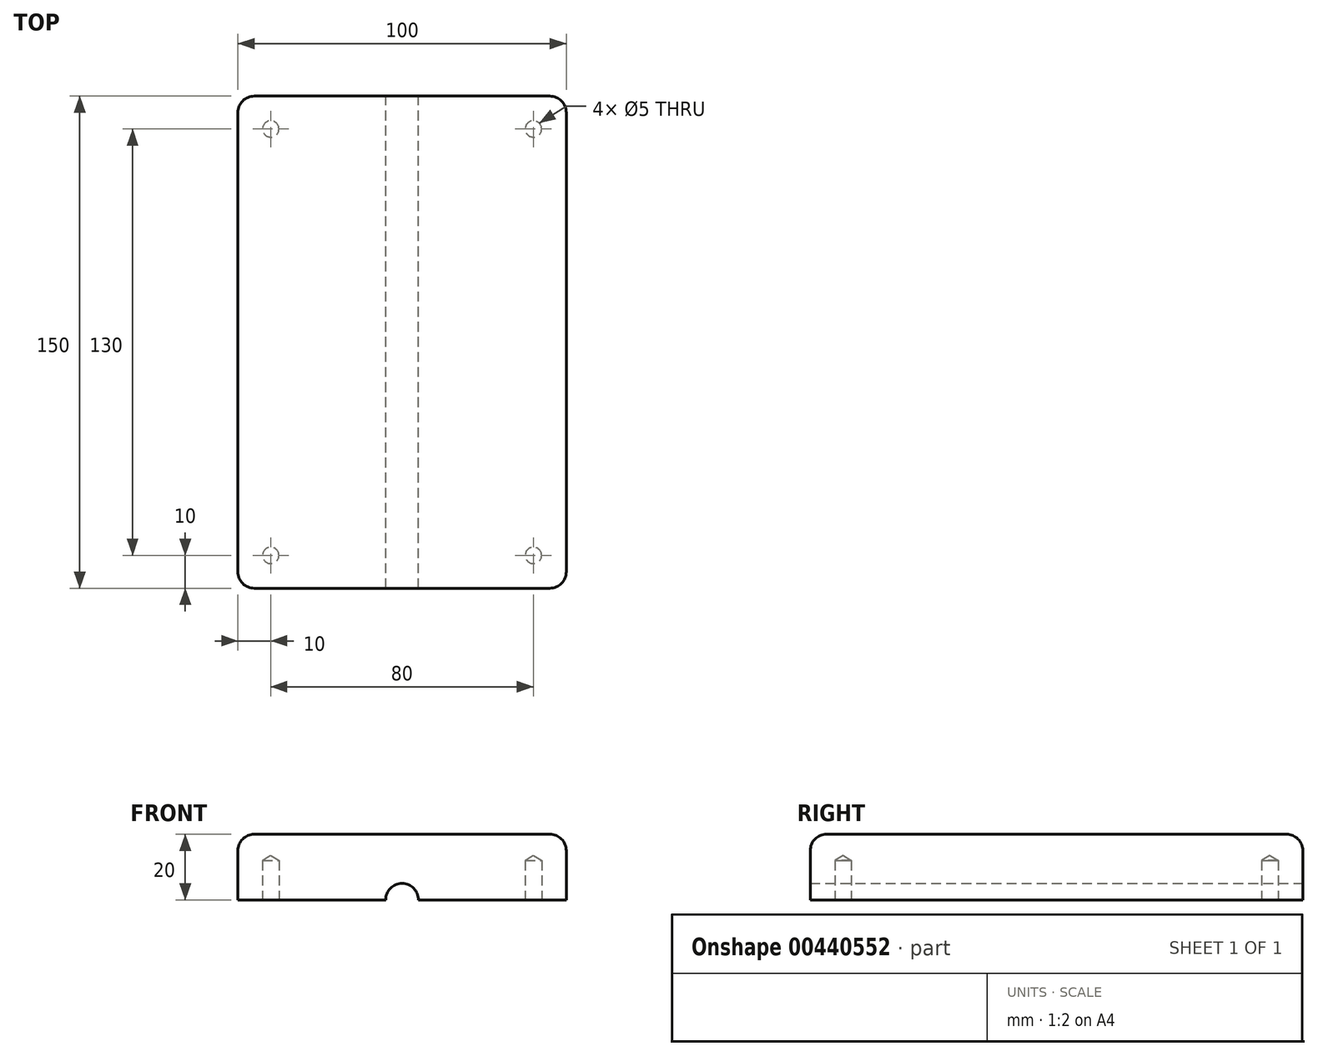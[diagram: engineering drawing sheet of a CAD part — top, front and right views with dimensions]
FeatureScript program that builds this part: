
annotation { "Feature Type Name" : "Feature", "Feature Type Description" : "" }
export const myFeature = defineFeature(function(context is Context, id is Id, definition is map)
    precondition{}
    {
        {
            var Q0;
            Q0=qCreatedBy(makeId("Top.planeOp"),FACE);
            var sketch = newSketch(context, id + "F0", { "sketchPlane" : qUnion([Q0])});
            skLineSegment(sketch, "E0.bottom", {"start": v(50, -75) * mm, "end": v(-50, -75) * mm});
            skLineSegment(sketch, "E0.top", {"start": v(50, 75) * mm, "end": v(-50, 75) * mm});
            skLineSegment(sketch, "E0.left", {"start": v(50, -75) * mm, "end": v(50, 75) * mm});
            skLineSegment(sketch, "E0.right", {"start": v(-50, -75) * mm, "end": v(-50, 75) * mm});
            skPoint(sketch, "E0.middle", {"position": v(0, 0) * mm});
            skPoint(sketch, "E1", {"position": v(-40, 65) * mm});
            skPoint(sketch, "E2", {"position": v(40, 65) * mm});
            skPoint(sketch, "E3", {"position": v(-40, -65) * mm});
            skPoint(sketch, "E4", {"position": v(40, -65) * mm});
            skSolve(sketch);
        }
        {
            var Q0;
            Q0=makeQuery(id+"F0.imprint","IMPRINT",FACE,{"disambiguationData":[TD([[makeQuery(id+"F0.imprint","IMPRINT",EDGE,{"derivedFrom":sQuery(id+"F0.wireOp",EDGE,"E0.bottom")}),-1.0]])]});
            extrude(context, id + "F1", {"entities" : qUnion([Q0]), "depth" : 20 * mm});
        }
        {
            var Q0;
            Q0=makeQuery(id+"F1.opExtrude","SWEPT_EDGE",EDGE,{"disambiguationData":[OSD([sQuery(id+"F0.wireOp",EDGE,"E0.top"),sQuery(id+"F0.wireOp",EDGE,"E0.right")])]});
            var Q1;
            Q1=makeQuery(id+"F1.opExtrude","SWEPT_EDGE",EDGE,{"disambiguationData":[OSD([sQuery(id+"F0.wireOp",EDGE,"E0.top"),sQuery(id+"F0.wireOp",EDGE,"E0.left")])]});
            var Q2;
            Q2=makeQuery(id+"F1.opExtrude","CAP_FACE",FACE,{"disambiguationData":[OSD([sQuery(id+"F0.wireOp",EDGE,"E0.bottom"),sQuery(id+"F0.wireOp",EDGE,"E0.top"),sQuery(id+"F0.wireOp",EDGE,"E0.left"),sQuery(id+"F0.wireOp",EDGE,"E0.right")])],"isStart":false});
            var Q3;
            Q3=makeQuery(id+"F1.opExtrude","SWEPT_EDGE",EDGE,{"disambiguationData":[OSD([sQuery(id+"F0.wireOp",EDGE,"E0.bottom"),sQuery(id+"F0.wireOp",EDGE,"E0.left")])]});
            var Q4;
            Q4=makeQuery(id+"F1.opExtrude","SWEPT_EDGE",EDGE,{"disambiguationData":[OSD([sQuery(id+"F0.wireOp",EDGE,"E0.bottom"),sQuery(id+"F0.wireOp",EDGE,"E0.right")])]});
            fillet(context, id + "F2", {"entities" : qUnion([Q0, Q1, Q2, Q3, Q4]), "radius" : 5 * mm, "tangentPropagation" : true, "allowEdgeOverflow" : false});
        }
        {
            var Q0;
            Q0=sQuery(id+"F0.wireOp",VERTEX,"E2");
            var Q1;
            Q1=sQuery(id+"F0.wireOp",VERTEX,"E1");
            var Q2;
            Q2=sQuery(id+"F0.wireOp",VERTEX,"E4");
            var Q3;
            Q3=sQuery(id+"F0.wireOp",VERTEX,"E3");
            var Q4;
            Q4=makeQuery(id+"F1.opExtrude","SWEPT_BODY",BODY,{"disambiguationData":[OSD([sQuery(id+"F0.wireOp",EDGE,"E0.bottom"),sQuery(id+"F0.wireOp",EDGE,"E0.top"),sQuery(id+"F0.wireOp",EDGE,"E0.left"),sQuery(id+"F0.wireOp",EDGE,"E0.right")])]});
            hole(context, id + "F3", {"style" : HoleStyle.SIMPLE, "endStyle" : HoleEndStyle.BLIND, "oppositeDirection" : true, "holeDiameter" : 5 * mm, "holeDepth" : 12 * mm, "isTappedThrough" : true, "tappedDepth" : 12 * mm, "tapClearance" : 3, "locations" : qUnion([Q0, Q1, Q2, Q3]), "scope" : qUnion([Q4])});
        }
        {
            var Q0;
            Q0=makeQuery(id+"F0.imprint","IMPRINT",FACE,{"disambiguationData":[TD([[makeQuery(id+"F0.imprint","IMPRINT",EDGE,{"derivedFrom":sQuery(id+"F0.wireOp",EDGE,"E0.bottom")}),-1.0]])]});
            var sketch = newSketch(context, id + "F4", { "sketchPlane" : qUnion([Q0])});
            skLineSegment(sketch, "E5.left", {"start": v(-5, -75) * mm, "end": v(-5, 75) * mm});
            skLineSegment(sketch, "E5.right", {"start": v(5, -75) * mm, "end": v(5, 75) * mm});
            skPoint(sketch, "E5.middle", {"position": v(0, 0) * mm});
            skLineSegment(sketch, "E6.0", {"start": v(50, -75) * mm, "end": v(-50, -75) * mm});
            skLineSegment(sketch, "E6.1", {"start": v(50, 75) * mm, "end": v(-50, 75) * mm});
            skSolve(sketch);
        }
        {
            var Q0;
            {var subQ0=sQuery(id+"F4.wireOp",EDGE,"E5.left");Q0=makeQuery(id+"F4.imprint","IMPRINT",FACE,{"disambiguationData":[TD([[makeQuery(id+"F4.imprint","IMPRINT",EDGE,{"derivedFrom":subQ0}),-1.0]])]});}
            extrude(context, id + "F5", {"entities" : qUnion([Q0]), "operationType" : NewBodyOperationType.REMOVE, "depth" : 5 * mm});
        }
        {
            var Q0;
            Q0=makeQuery(id+"F5.boolean.opBoolean","COPY",EDGE,{"derivedFrom":makeQuery(id+"F5.opExtrude","CAP_EDGE",EDGE,{"disambiguationData":[OSD([sQuery(id+"F4.wireOp",EDGE,"E5.right")])],"isStart":false})});
            var Q1;
            Q1=makeQuery(id+"F5.boolean.opBoolean","COPY",EDGE,{"derivedFrom":makeQuery(id+"F5.opExtrude","CAP_EDGE",EDGE,{"disambiguationData":[OSD([sQuery(id+"F4.wireOp",EDGE,"E5.left")])],"isStart":false})});
            var Q2;
            Q2=makeQuery(id+"F5.boolean.opBoolean","COPY",EDGE,{"derivedFrom":makeQuery(id+"F5.opExtrude","SWEPT_EDGE",EDGE,{"disambiguationData":[OSD([sQuery(id+"F4.wireOp",EDGE,"E5.right"),sQuery(id+"F4.wireOp",EDGE,"E6.0")])]})});
            var Q3;
            Q3=makeQuery(id+"F5.boolean.opBoolean","COPY",EDGE,{"derivedFrom":makeQuery(id+"F5.opExtrude","SWEPT_EDGE",EDGE,{"disambiguationData":[OSD([sQuery(id+"F4.wireOp",EDGE,"E5.left"),sQuery(id+"F4.wireOp",EDGE,"E6.1")])]})});
            fillet(context, id + "F6", {"entities" : qUnion([Q0, Q1, Q2, Q3]), "radius" : 5 * mm, "tangentPropagation" : true, "allowEdgeOverflow" : false});
        }
    });
